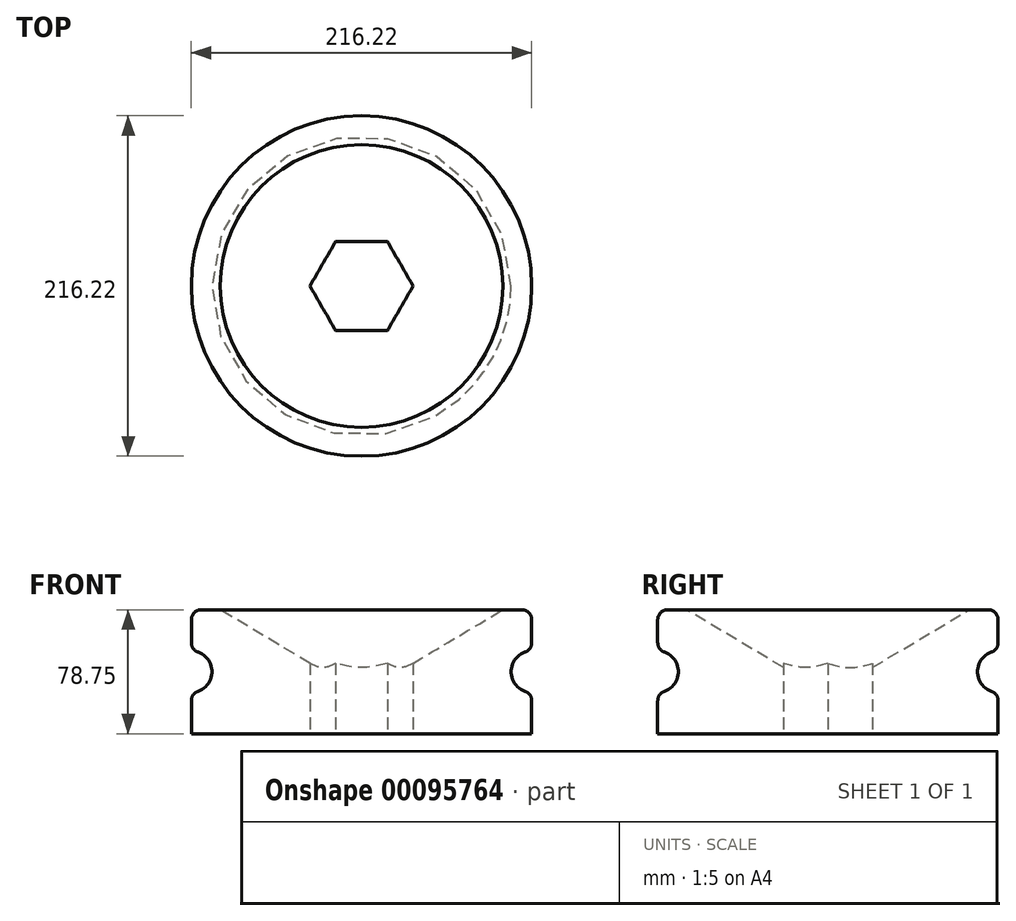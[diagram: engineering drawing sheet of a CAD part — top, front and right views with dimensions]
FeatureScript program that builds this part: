
annotation { "Feature Type Name" : "Feature", "Feature Type Description" : "" }
export const myFeature = defineFeature(function(context is Context, id is Id, definition is map)
    precondition{}
    {
        {
            var Q0;
            Q0=qCreatedBy(makeId("Front.planeOp"),FACE);
            var sketch = newSketch(context, id + "F0", { "sketchPlane" : qUnion([Q0])});
            skLineSegment(sketch, "E0", {"start": v(0, 0) * mm, "end": v(108.1, 0) * mm});
            skLineSegment(sketch, "E1", {"start": v(108.1, 0) * mm, "end": v(108.1, 20.94) * mm});
            skLineSegment(sketch, "E2", {"start": v(101.76, 78.75) * mm, "end": v(89.7, 78.75) * mm});
            skLineSegment(sketch, "E3", {"start": v(89.7, 78.75) * mm, "end": v(3.1, 26.99) * mm});
            skLineSegment(sketch, "E4", {"start": v(0, 21.54) * mm, "end": v(0, 0) * mm});
            skArc(sketch, "E5", {"start": v(103.82, 51.81) * mm, "mid": v(94.95, 39.38) * mm, "end": v(103.82, 26.94) * mm});
            skLineSegment(sketch, "E6.trimOffspring", {"start": v(108.1, 57.82) * mm, "end": v(108.1, 72.4) * mm});
            skPoint(sketch, "E7.visualSharp", {"position": v(108.1, 52.53) * mm});
            skArc(sketch, "E7.filletArc", {"start": v(103.82, 51.81) * mm, "mid": v(106.92, 54.13) * mm, "end": v(108.1, 57.82) * mm});
            skPoint(sketch, "E8.visualSharp", {"position": v(108.1, 26.22) * mm});
            skArc(sketch, "E8.filletArc", {"start": v(108.1, 20.94) * mm, "mid": v(106.92, 24.62) * mm, "end": v(103.82, 26.94) * mm});
            skPoint(sketch, "E9.visualSharp", {"position": v(108.1, 78.75) * mm});
            skArc(sketch, "E9.filletArc", {"start": v(108.1, 72.4) * mm, "mid": v(106.25, 76.9) * mm, "end": v(101.76, 78.75) * mm});
            skPoint(sketch, "E10.visualSharp", {"position": v(0, 25.14) * mm});
            skArc(sketch, "E10.filletArc", {"start": v(3.1, 26.99) * mm, "mid": v(0.83, 24.67) * mm, "end": v(0, 21.54) * mm});
            skLineSegment(sketch, "E11", {"start": v(0, 69.82) * mm, "end": v(0, -34.26) * mm, "construction": true});
            skSolve(sketch);
        }
        {
            var Q0;
            Q0 = qSketchRegion(id + "F0", true);
            var Q1;
            Q1=sQuery(id+"F0.wireOp",EDGE,"E11");
            revolve(context, id + "F1", {"entities" : qUnion([Q0]), "axis" : qUnion([Q1]), "revolveType" : RevolveType.FULL});
        }
        {
            var Q0;
            Q0=makeQuery(id+"F1.opRevolve","SWEPT_FACE",FACE,{"disambiguationData":[OSD([sQuery(id+"F0.wireOp",EDGE,"E0")])]});
            var sketch = newSketch(context, id + "F2", { "sketchPlane" : qUnion([Q0])});
            skCircle(sketch, "E12.cCircle", {"center": v(0, 0) * mm, "radius": 28.38 * mm, "construction": true});
            skLineSegment(sketch, "E12.0", {"start": v(-16.38, 28.38) * mm, "end": v(16.38, 28.38) * mm});
            skLineSegment(sketch, "E12.1", {"start": v(16.38, 28.38) * mm, "end": v(32.77, 0) * mm});
            skLineSegment(sketch, "E12.2", {"start": v(32.77, 0) * mm, "end": v(16.38, -28.38) * mm});
            skLineSegment(sketch, "E12.3", {"start": v(16.38, -28.38) * mm, "end": v(-16.38, -28.38) * mm});
            skLineSegment(sketch, "E12.4", {"start": v(-16.38, -28.38) * mm, "end": v(-32.77, 0) * mm});
            skLineSegment(sketch, "E12.5", {"start": v(-32.77, 0) * mm, "end": v(-16.38, 28.38) * mm});
            skPoint(sketch, "E12.0.midPoint", {"position": v(0, 28.38) * mm});
            skSolve(sketch);
        }
        {
            var Q0;
            Q0 = qSketchRegion(id + "F2", true);
            extrude(context, id + "F3", {"entities" : qUnion([Q0]), "operationType" : NewBodyOperationType.REMOVE, "oppositeDirection" : true, "depth" : 175.35 * mm});
        }
    });
